FCSTD DOCUMENT  (FreeCAD 1.0R39319 (Git))
Label: Medical_Clinic_Layout1
License: All rights reserved
LicenseURL: https://en.wikipedia.org/wiki/All_rights_reserved
objects: App::FeaturePython×33, Part::Part2DObjectPython×31
note: 31 computed .brp shape members not serialized (recipe doc carries the construction recipe); baked Part::Feature solids carry a one-line shape summary decoded from their .brp

FEATURE [Part::Part2DObjectPython] Wire  # Draft 2D object (typed FeaturePython)
  Area = 308000000
  ChamferSize = 0
  Closed = true
  End = (0,0,0)
  FilletRadius = 0
  Length = 72000
  MakeFace = true
  Points = (5) [(0,0,0),(22000,0,0),(22000,14000,0),(0,14000,0),(0,0,0)]
  Start = (0,0,0)
  Subdivisions = 0
FEATURE [Part::Part2DObjectPython] Rectangle  # Draft 2D object (typed FeaturePython)
  Area = 1.2e+07
  ChamferSize = 0
  Columns = 1
  FilletRadius = 0
  Height = 3000
  Length = 4000
  MakeFace = true
  Placement = pos=(1000,1000,0) rot=(0,0,1;0rad)
  Rows = 1
FEATURE [App::FeaturePython] Text  # WARN: FeaturePython — macro-defined, semantics opaque (R4)
  Placement = pos=(2333,2500,0) rot=(0,0,1;0rad)
  Text = Reception | 12 sqm
FEATURE [Part::Part2DObjectPython] Rectangle001  # Draft 2D object (typed FeaturePython)
  Area = 4e+07
  ChamferSize = 0
  Columns = 1
  FilletRadius = 0
  Height = 5000
  Length = 8000
  MakeFace = true
  Placement = pos=(6000,1000,0) rot=(0,0,1;0rad)
  Rows = 1
FEATURE [App::FeaturePython] Text001  # WARN: FeaturePython — macro-defined, semantics opaque (R4)
  Placement = pos=(8666,3500,0) rot=(0,0,1;0rad)
  Text = Waiting Area | 40 sqm
FEATURE [Part::Part2DObjectPython] Rectangle002  # Draft 2D object (typed FeaturePython)
  Area = 18000000
  ChamferSize = 0
  Columns = 1
  FilletRadius = 0
  Height = 4000
  Length = 4500
  MakeFace = true
  Placement = pos=(1000,5000,0) rot=(0,0,1;0rad)
  Rows = 1
FEATURE [App::FeaturePython] Text002  # WARN: FeaturePython — macro-defined, semantics opaque (R4)
  Placement = pos=(2500,7000,0) rot=(0,0,1;0rad)
  Text = Consultation Room 1 | 18 sqm
FEATURE [Part::Part2DObjectPython] Rectangle003  # Draft 2D object (typed FeaturePython)
  Area = 18000000
  ChamferSize = 0
  Columns = 1
  FilletRadius = 0
  Height = 4000
  Length = 4500
  MakeFace = true
  Placement = pos=(6500,5000,0) rot=(0,0,1;0rad)
  Rows = 1
FEATURE [App::FeaturePython] Text003  # WARN: FeaturePython — macro-defined, semantics opaque (R4)
  Placement = pos=(8000,7000,0) rot=(0,0,1;0rad)
  Text = Consultation Room 2 | 18 sqm
FEATURE [Part::Part2DObjectPython] Rectangle004  # Draft 2D object (typed FeaturePython)
  Area = 18000000
  ChamferSize = 0
  Columns = 1
  FilletRadius = 0
  Height = 4000
  Length = 4500
  MakeFace = true
  Placement = pos=(12000,5000,0) rot=(0,0,1;0rad)
  Rows = 1
FEATURE [App::FeaturePython] Text004  # WARN: FeaturePython — macro-defined, semantics opaque (R4)
  Placement = pos=(13500,7000,0) rot=(0,0,1;0rad)
  Text = Consultation Room 3 | 18 sqm
FEATURE [Part::Part2DObjectPython] Rectangle005  # Draft 2D object (typed FeaturePython)
  Area = 20000000
  ChamferSize = 0
  Columns = 1
  FilletRadius = 0
  Height = 4000
  Length = 5000
  MakeFace = true
  Placement = pos=(17000,1000,0) rot=(0,0,1;0rad)
  Rows = 1
FEATURE [App::FeaturePython] Text005  # WARN: FeaturePython — macro-defined, semantics opaque (R4)
  Placement = pos=(18666,3000,0) rot=(0,0,1;0rad)
  Text = Pharmacy | 20 sqm
FEATURE [Part::Part2DObjectPython] Rectangle006  # Draft 2D object (typed FeaturePython)
  Area = 30000000
  ChamferSize = 0
  Columns = 1
  FilletRadius = 0
  Height = 5000
  Length = 6000
  MakeFace = true
  Placement = pos=(1000,10000,0) rot=(0,0,1;0rad)
  Rows = 1
FEATURE [App::FeaturePython] Text006  # WARN: FeaturePython — macro-defined, semantics opaque (R4)
  Placement = pos=(3000,12500,0) rot=(0,0,1;0rad)
  Text = Laboratory | 30 sqm
FEATURE [Part::Part2DObjectPython] Rectangle007  # Draft 2D object (typed FeaturePython)
  Area = 7500000
  ChamferSize = 0
  Columns = 1
  FilletRadius = 0
  Height = 2500
  Length = 3000
  MakeFace = true
  Placement = pos=(8000,10000,0) rot=(0,0,1;0rad)
  Rows = 1
FEATURE [App::FeaturePython] Text007  # WARN: FeaturePython — macro-defined, semantics opaque (R4)
  Placement = pos=(9000,11250,0) rot=(0,0,1;0rad)
  Text = Sample Collection | 7.5 sqm
FEATURE [Part::Part2DObjectPython] Rectangle008  # Draft 2D object (typed FeaturePython)
  Area = 7500000
  ChamferSize = 0
  Columns = 1
  FilletRadius = 0
  Height = 2500
  Length = 3000
  MakeFace = true
  Placement = pos=(12000,10000,0) rot=(0,0,1;0rad)
  Rows = 1
FEATURE [App::FeaturePython] Text008  # WARN: FeaturePython — macro-defined, semantics opaque (R4)
  Placement = pos=(13000,11250,0) rot=(0,0,1;0rad)
  Text = Staff Room | 7.5 sqm
FEATURE [Part::Part2DObjectPython] Rectangle009  # Draft 2D object (typed FeaturePython)
  Area = 1.2e+07
  ChamferSize = 0
  Columns = 1
  FilletRadius = 0
  Height = 3000
  Length = 4000
  MakeFace = true
  Placement = pos=(16000,10000,0) rot=(0,0,1;0rad)
  Rows = 1
FEATURE [App::FeaturePython] Text009  # WARN: FeaturePython — macro-defined, semantics opaque (R4)
  Placement = pos=(17333,11500,0) rot=(0,0,1;0rad)
  Text = Restrooms | 12 sqm
FEATURE [App::FeaturePython] Dimension  # Draft dimension (typed FeaturePython)
  Diameter = false
  Dimline = (11000,-800,0)
  Direction = (0,0,0)
  Distance = 22000
  End = (22000,-800,0)
  Normal = (0,0,1)
  Start = (0,-800,0)
FEATURE [App::FeaturePython] Dimension001  # Draft dimension (typed FeaturePython)
  Diameter = false
  Dimline = (-800,7000,0)
  Direction = (0,0,0)
  Distance = 14000
  End = (-800,14000,0)
  Normal = (0,0,1)
  Start = (-800,0,0)
FEATURE [Part::Part2DObjectPython] Line  # Draft 2D object (typed FeaturePython)
  Area = 0
  ChamferSize = 0
  Closed = false
  End = (0,15500,0)
  FilletRadius = 0
  Length = 17000
  MakeFace = true
  Points = (2) [(0,-1500,0),(0,15500,0)]
  Start = (0,-1500,0)
  Subdivisions = 0
FEATURE [App::FeaturePython] Text010  # WARN: FeaturePython — macro-defined, semantics opaque (R4)
  Placement = pos=(-100,-2000,0) rot=(0,0,1;0rad)
  Text = A
FEATURE [Part::Part2DObjectPython] Line001  # Draft 2D object (typed FeaturePython)
  Area = 0
  ChamferSize = 0
  Closed = false
  End = (2000,15500,0)
  FilletRadius = 0
  Length = 17000
  MakeFace = true
  Points = (2) [(2000,-1500,0),(2000,15500,0)]
  Start = (2000,-1500,0)
  Subdivisions = 0
FEATURE [App::FeaturePython] Text011  # WARN: FeaturePython — macro-defined, semantics opaque (R4)
  Placement = pos=(1900,-2000,0) rot=(0,0,1;0rad)
  Text = B
FEATURE [Part::Part2DObjectPython] Line002  # Draft 2D object (typed FeaturePython)
  Area = 0
  ChamferSize = 0
  Closed = false
  End = (4000,15500,0)
  FilletRadius = 0
  Length = 17000
  MakeFace = true
  Points = (2) [(4000,-1500,0),(4000,15500,0)]
  Start = (4000,-1500,0)
  Subdivisions = 0
FEATURE [App::FeaturePython] Text012  # WARN: FeaturePython — macro-defined, semantics opaque (R4)
  Placement = pos=(3900,-2000,0) rot=(0,0,1;0rad)
  Text = C
FEATURE [Part::Part2DObjectPython] Line003  # Draft 2D object (typed FeaturePython)
  Area = 0
  ChamferSize = 0
  Closed = false
  End = (6000,15500,0)
  FilletRadius = 0
  Length = 17000
  MakeFace = true
  Points = (2) [(6000,-1500,0),(6000,15500,0)]
  Start = (6000,-1500,0)
  Subdivisions = 0
FEATURE [App::FeaturePython] Text013  # WARN: FeaturePython — macro-defined, semantics opaque (R4)
  Placement = pos=(5900,-2000,0) rot=(0,0,1;0rad)
  Text = D
FEATURE [Part::Part2DObjectPython] Line004  # Draft 2D object (typed FeaturePython)
  Area = 0
  ChamferSize = 0
  Closed = false
  End = (8000,15500,0)
  FilletRadius = 0
  Length = 17000
  MakeFace = true
  Points = (2) [(8000,-1500,0),(8000,15500,0)]
  Start = (8000,-1500,0)
  Subdivisions = 0
FEATURE [App::FeaturePython] Text014  # WARN: FeaturePython — macro-defined, semantics opaque (R4)
  Placement = pos=(7900,-2000,0) rot=(0,0,1;0rad)
  Text = E
FEATURE [Part::Part2DObjectPython] Line005  # Draft 2D object (typed FeaturePython)
  Area = 0
  ChamferSize = 0
  Closed = false
  End = (10000,15500,0)
  FilletRadius = 0
  Length = 17000
  MakeFace = true
  Points = (2) [(10000,-1500,0),(10000,15500,0)]
  Start = (10000,-1500,0)
  Subdivisions = 0
FEATURE [App::FeaturePython] Text015  # WARN: FeaturePython — macro-defined, semantics opaque (R4)
  Placement = pos=(9900,-2000,0) rot=(0,0,1;0rad)
  Text = F
FEATURE [Part::Part2DObjectPython] Line006  # Draft 2D object (typed FeaturePython)
  Area = 0
  ChamferSize = 0
  Closed = false
  End = (12000,15500,0)
  FilletRadius = 0
  Length = 17000
  MakeFace = true
  Points = (2) [(12000,-1500,0),(12000,15500,0)]
  Start = (12000,-1500,0)
  Subdivisions = 0
FEATURE [App::FeaturePython] Text016  # WARN: FeaturePython — macro-defined, semantics opaque (R4)
  Placement = pos=(11900,-2000,0) rot=(0,0,1;0rad)
  Text = G
FEATURE [Part::Part2DObjectPython] Line007  # Draft 2D object (typed FeaturePython)
  Area = 0
  ChamferSize = 0
  Closed = false
  End = (14000,15500,0)
  FilletRadius = 0
  Length = 17000
  MakeFace = true
  Points = (2) [(14000,-1500,0),(14000,15500,0)]
  Start = (14000,-1500,0)
  Subdivisions = 0
FEATURE [App::FeaturePython] Text017  # WARN: FeaturePython — macro-defined, semantics opaque (R4)
  Placement = pos=(13900,-2000,0) rot=(0,0,1;0rad)
  Text = H
FEATURE [Part::Part2DObjectPython] Line008  # Draft 2D object (typed FeaturePython)
  Area = 0
  ChamferSize = 0
  Closed = false
  End = (16000,15500,0)
  FilletRadius = 0
  Length = 17000
  MakeFace = true
  Points = (2) [(16000,-1500,0),(16000,15500,0)]
  Start = (16000,-1500,0)
  Subdivisions = 0
FEATURE [App::FeaturePython] Text018  # WARN: FeaturePython — macro-defined, semantics opaque (R4)
  Placement = pos=(15900,-2000,0) rot=(0,0,1;0rad)
  Text = I
FEATURE [Part::Part2DObjectPython] Line009  # Draft 2D object (typed FeaturePython)
  Area = 0
  ChamferSize = 0
  Closed = false
  End = (18000,15500,0)
  FilletRadius = 0
  Length = 17000
  MakeFace = true
  Points = (2) [(18000,-1500,0),(18000,15500,0)]
  Start = (18000,-1500,0)
  Subdivisions = 0
FEATURE [App::FeaturePython] Text019  # WARN: FeaturePython — macro-defined, semantics opaque (R4)
  Placement = pos=(17900,-2000,0) rot=(0,0,1;0rad)
  Text = J
FEATURE [Part::Part2DObjectPython] Line010  # Draft 2D object (typed FeaturePython)
  Area = 0
  ChamferSize = 0
  Closed = false
  End = (20000,15500,0)
  FilletRadius = 0
  Length = 17000
  MakeFace = true
  Points = (2) [(20000,-1500,0),(20000,15500,0)]
  Start = (20000,-1500,0)
  Subdivisions = 0
FEATURE [App::FeaturePython] Text020  # WARN: FeaturePython — macro-defined, semantics opaque (R4)
  Placement = pos=(19900,-2000,0) rot=(0,0,1;0rad)
  Text = K
FEATURE [Part::Part2DObjectPython] Line011  # Draft 2D object (typed FeaturePython)
  Area = 0
  ChamferSize = 0
  Closed = false
  End = (22000,15500,0)
  FilletRadius = 0
  Length = 17000
  MakeFace = true
  Points = (2) [(22000,-1500,0),(22000,15500,0)]
  Start = (22000,-1500,0)
  Subdivisions = 0
FEATURE [App::FeaturePython] Text021  # WARN: FeaturePython — macro-defined, semantics opaque (R4)
  Placement = pos=(21900,-2000,0) rot=(0,0,1;0rad)
  Text = L
FEATURE [Part::Part2DObjectPython] Line012  # Draft 2D object (typed FeaturePython)
  Area = 0
  ChamferSize = 0
  Closed = false
  End = (23500,0,0)
  FilletRadius = 0
  Length = 25000
  MakeFace = true
  Points = (2) [(-1500,0,0),(23500,0,0)]
  Start = (-1500,0,0)
  Subdivisions = 0
FEATURE [App::FeaturePython] Text022  # WARN: FeaturePython — macro-defined, semantics opaque (R4)
  Placement = pos=(-2200,-100,0) rot=(0,0,1;0rad)
  Text = 1
FEATURE [Part::Part2DObjectPython] Line013  # Draft 2D object (typed FeaturePython)
  Area = 0
  ChamferSize = 0
  Closed = false
  End = (23500,2000,0)
  FilletRadius = 0
  Length = 25000
  MakeFace = true
  Points = (2) [(-1500,2000,0),(23500,2000,0)]
  Start = (-1500,2000,0)
  Subdivisions = 0
FEATURE [App::FeaturePython] Text023  # WARN: FeaturePython — macro-defined, semantics opaque (R4)
  Placement = pos=(-2200,1900,0) rot=(0,0,1;0rad)
  Text = 2
FEATURE [Part::Part2DObjectPython] Line014  # Draft 2D object (typed FeaturePython)
  Area = 0
  ChamferSize = 0
  Closed = false
  End = (23500,4000,0)
  FilletRadius = 0
  Length = 25000
  MakeFace = true
  Points = (2) [(-1500,4000,0),(23500,4000,0)]
  Start = (-1500,4000,0)
  Subdivisions = 0
FEATURE [App::FeaturePython] Text024  # WARN: FeaturePython — macro-defined, semantics opaque (R4)
  Placement = pos=(-2200,3900,0) rot=(0,0,1;0rad)
  Text = 3
FEATURE [Part::Part2DObjectPython] Line015  # Draft 2D object (typed FeaturePython)
  Area = 0
  ChamferSize = 0
  Closed = false
  End = (23500,6000,0)
  FilletRadius = 0
  Length = 25000
  MakeFace = true
  Points = (2) [(-1500,6000,0),(23500,6000,0)]
  Start = (-1500,6000,0)
  Subdivisions = 0
FEATURE [App::FeaturePython] Text025  # WARN: FeaturePython — macro-defined, semantics opaque (R4)
  Placement = pos=(-2200,5900,0) rot=(0,0,1;0rad)
  Text = 4
FEATURE [Part::Part2DObjectPython] Line016  # Draft 2D object (typed FeaturePython)
  Area = 0
  ChamferSize = 0
  Closed = false
  End = (23500,8000,0)
  FilletRadius = 0
  Length = 25000
  MakeFace = true
  Points = (2) [(-1500,8000,0),(23500,8000,0)]
  Start = (-1500,8000,0)
  Subdivisions = 0
FEATURE [App::FeaturePython] Text026  # WARN: FeaturePython — macro-defined, semantics opaque (R4)
  Placement = pos=(-2200,7900,0) rot=(0,0,1;0rad)
  Text = 5
FEATURE [Part::Part2DObjectPython] Line017  # Draft 2D object (typed FeaturePython)
  Area = 0
  ChamferSize = 0
  Closed = false
  End = (23500,10000,0)
  FilletRadius = 0
  Length = 25000
  MakeFace = true
  Points = (2) [(-1500,10000,0),(23500,10000,0)]
  Start = (-1500,10000,0)
  Subdivisions = 0
FEATURE [App::FeaturePython] Text027  # WARN: FeaturePython — macro-defined, semantics opaque (R4)
  Placement = pos=(-2200,9900,0) rot=(0,0,1;0rad)
  Text = 6
FEATURE [Part::Part2DObjectPython] Line018  # Draft 2D object (typed FeaturePython)
  Area = 0
  ChamferSize = 0
  Closed = false
  End = (23500,12000,0)
  FilletRadius = 0
  Length = 25000
  MakeFace = true
  Points = (2) [(-1500,12000,0),(23500,12000,0)]
  Start = (-1500,12000,0)
  Subdivisions = 0
FEATURE [App::FeaturePython] Text028  # WARN: FeaturePython — macro-defined, semantics opaque (R4)
  Placement = pos=(-2200,11900,0) rot=(0,0,1;0rad)
  Text = 7
FEATURE [Part::Part2DObjectPython] Line019  # Draft 2D object (typed FeaturePython)
  Area = 0
  ChamferSize = 0
  Closed = false
  End = (23500,14000,0)
  FilletRadius = 0
  Length = 25000
  MakeFace = true
  Points = (2) [(-1500,14000,0),(23500,14000,0)]
  Start = (-1500,14000,0)
  Subdivisions = 0
FEATURE [App::FeaturePython] Text029  # WARN: FeaturePython — macro-defined, semantics opaque (R4)
  Placement = pos=(-2200,13900,0) rot=(0,0,1;0rad)
  Text = 8
FEATURE [App::FeaturePython] Text030  # WARN: FeaturePython — macro-defined, semantics opaque (R4)
  Placement = pos=(16000,-2500,0) rot=(0,0,1;0rad)
  Text = Medical Clinic Layout | Scale: 1:100 | Total Area: 280 sqm
